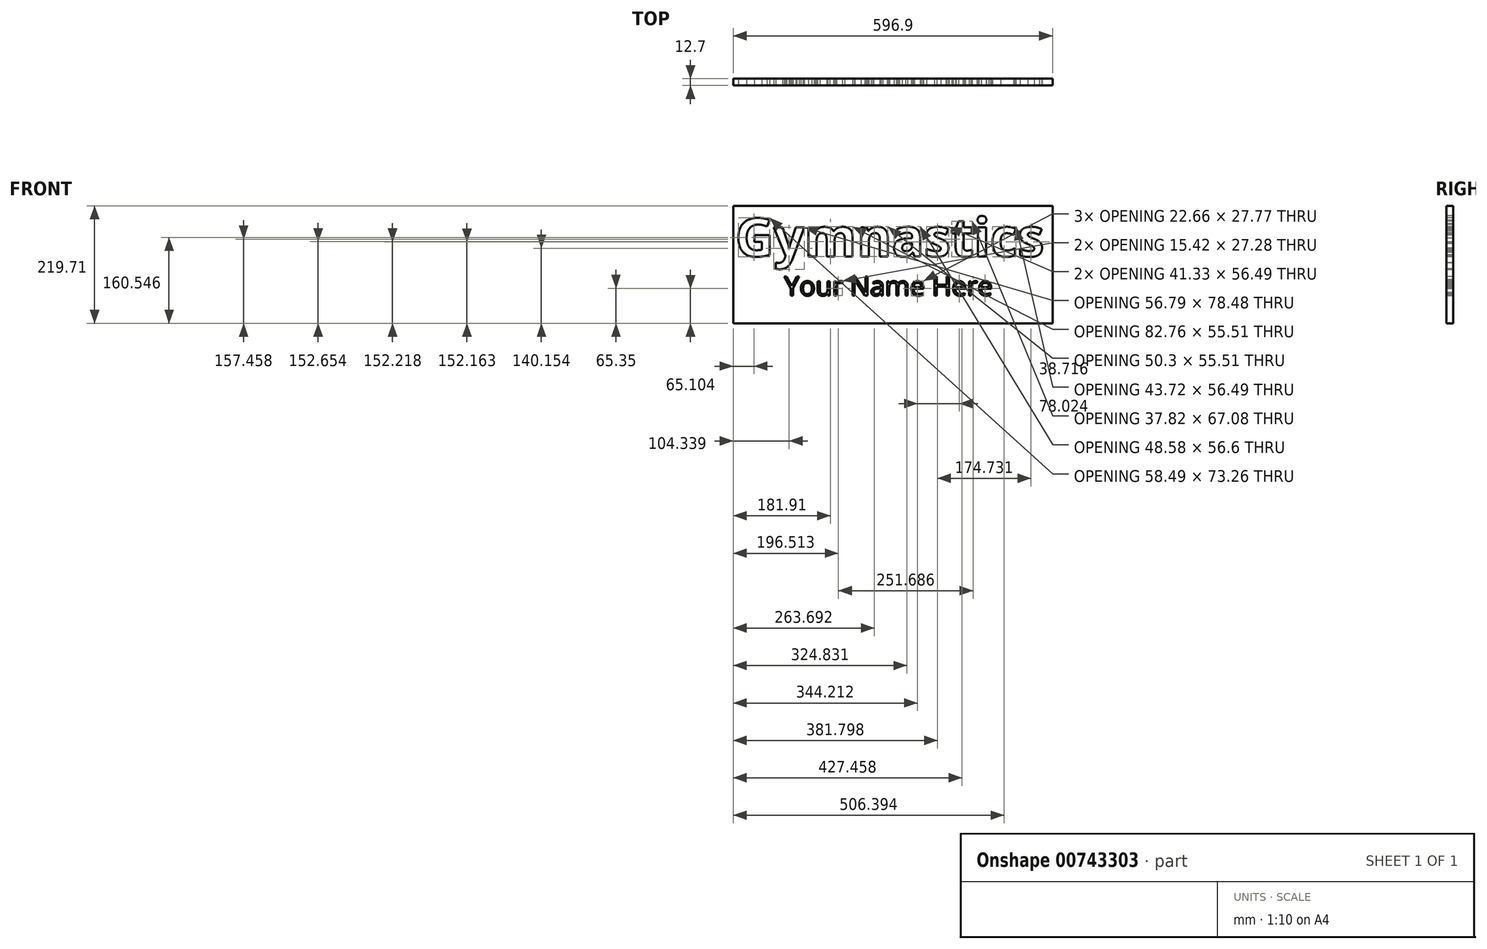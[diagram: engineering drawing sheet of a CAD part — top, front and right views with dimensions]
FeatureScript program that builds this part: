
annotation { "Feature Type Name" : "Feature", "Feature Type Description" : "" }
export const myFeature = defineFeature(function(context is Context, id is Id, definition is map)
    precondition{}
    {
        {
            var Q0;
            Q0=qCreatedBy(makeId("Front.planeOp"),FACE);
            var sketch = newSketch(context, id + "F0", { "sketchPlane" : qUnion([Q0])});
            skLineSegment(sketch, "E0.bottom", {"start": v(-290.57, 105.94) * mm, "end": v(306.33, 105.94) * mm});
            skLineSegment(sketch, "E0.top", {"start": v(-290.57, -113.77) * mm, "end": v(306.33, -113.77) * mm});
            skLineSegment(sketch, "E0.left", {"start": v(-290.57, 105.94) * mm, "end": v(-290.57, -113.77) * mm});
            skLineSegment(sketch, "E0.right", {"start": v(306.33, 105.94) * mm, "end": v(306.33, -113.77) * mm});
            skSolve(sketch);
        }
        {
            var Q0;
            Q0=makeQuery(id+"F0.imprint","IMPRINT",FACE,{"disambiguationData":[TD([[makeQuery(id+"F0.imprint","IMPRINT",EDGE,{"derivedFrom":sQuery(id+"F0.wireOp",EDGE,"E0.bottom")}),-1.0]])]});
            extrude(context, id + "F1", {"entities" : qUnion([Q0]), "depth" : 12.7 * mm, "offsetDistance" : 25.4 * mm});
        }
        {
            var Q0;
            Q0=makeQuery(id+"F1.opExtrude","CAP_FACE",FACE,{"disambiguationData":[OSD([sQuery(id+"F0.wireOp",EDGE,"E0.bottom"),sQuery(id+"F0.wireOp",EDGE,"E0.top"),sQuery(id+"F0.wireOp",EDGE,"E0.left"),sQuery(id+"F0.wireOp",EDGE,"E0.right")])],"isStart":false});
            var sketch = newSketch(context, id + "F2", { "sketchPlane" : qUnion([Q0])});
            skText(sketch, "E1", { "text": "Gymnastics", "fontName": "OpenSans-Bold.ttf"});
            const initialGuessF2  = {"E1": [-0.2869, 0.01113, 1, 0, 0.07187]};
            skSetInitialGuess(sketch, initialGuessF2);
            skSolve(sketch);
        }
        {
            var Q0;
            Q0=makeQuery(id+"F2.imprint","IMPRINT",FACE,{"disambiguationData":[TD([[makeQuery(id+"F2.imprint","IMPRINT",EDGE,{"derivedFrom":sQuery(id+"F2.wireOp",EDGE,"E1.sketch_text.stroke-0")}),1.0]])]});
            var sketch = newSketch(context, id + "F3", { "sketchPlane" : qUnion([Q0])});
            skText(sketch, "E2", { "text": "Your Name Here", "fontName": "OpenSans-Regular.ttf"});
            const initialGuessF3  = {"E2": [-0.19506, -0.06206, 1, 0, 0.03604]};
            skSetInitialGuess(sketch, initialGuessF3);
            skSolve(sketch);
        }
        {
            var Q0;
            Q0 = qSketchRegion(id + "F2", true);
            var Q1;
            Q1 = qSketchRegion(id + "F3", true);
            extrude(context, id + "F4", {"entities" : qUnion([Q0, Q1]), "operationType" : NewBodyOperationType.REMOVE, "oppositeDirection" : true, "depth" : 25.4 * mm, "offsetDistance" : 25.4 * mm});
        }
    });
